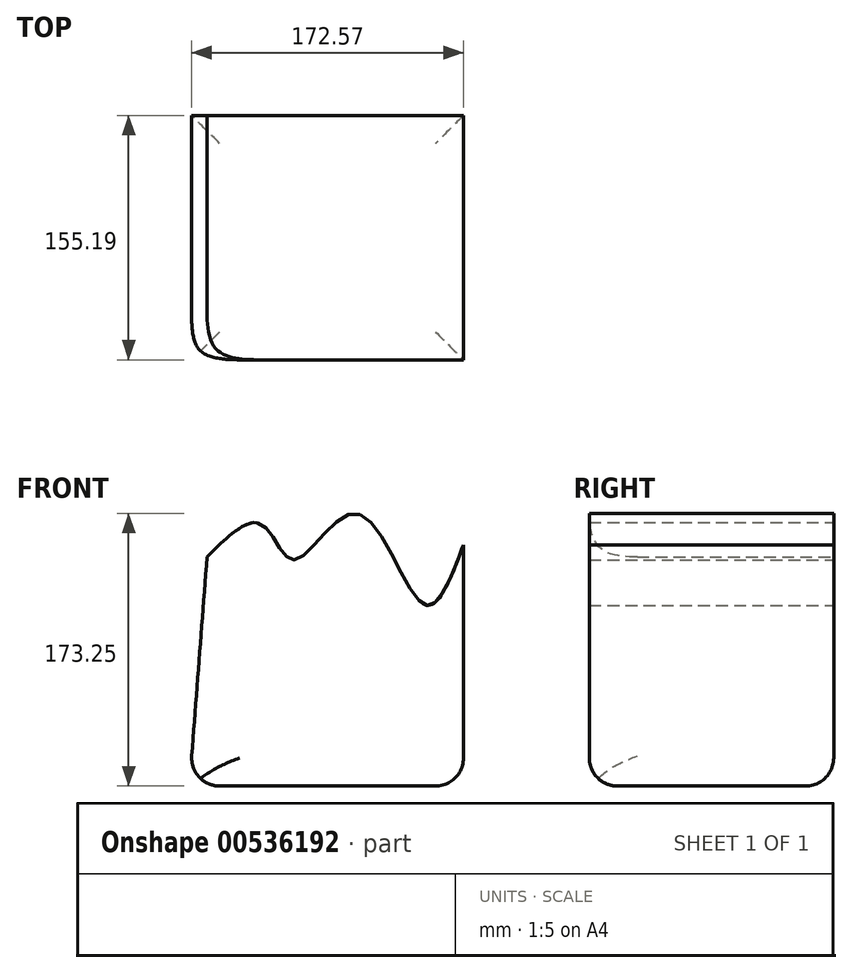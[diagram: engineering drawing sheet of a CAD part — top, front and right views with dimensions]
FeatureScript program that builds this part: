
annotation { "Feature Type Name" : "Feature", "Feature Type Description" : "" }
export const myFeature = defineFeature(function(context is Context, id is Id, definition is map)
    precondition{}
    {
        {
            var Q0;
            Q0=qCreatedBy(makeId("Front.planeOp"),FACE);
            var sketch = newSketch(context, id + "F0", { "sketchPlane" : qUnion([Q0])});
            skFitSpline(sketch, "E0", {"points": [v(-120.22, 34.32) * mm, v(-85.27, 54.9) * mm, v(-65, 32.43) * mm, v(-25.51, 62) * mm, v(17.12, 4.42) * mm, v(42.64, 41.84) * mm], "startDerivative": vector(209.05, 207.88) * mm, "endDerivative": vector(122.06, 324.77) * mm});
            skLineSegment(sketch, "E1", {"start": v(42.64, 41.84) * mm, "end": v(42.64, -111.18) * mm});
            skLineSegment(sketch, "E2", {"start": v(42.64, -111.18) * mm, "end": v(-131.34, -111.18) * mm});
            skLineSegment(sketch, "E3", {"start": v(-131.34, -111.18) * mm, "end": v(-120.22, 34.32) * mm});
            skSolve(sketch);
        }
        {
            var Q0;
            Q0=makeQuery(id+"F0.imprint","IMPRINT",FACE,{"disambiguationData":[TD([[makeQuery(id+"F0.imprint","IMPRINT",EDGE,{"derivedFrom":sQuery(id+"F0.wireOp",EDGE,"E0")}),-1.0]])]});
            extrude(context, id + "F1", {"entities" : qUnion([Q0]), "depth" : 155.2 * mm, "offsetDistance" : 25.4 * mm});
        }
        {
            var Q0;
            Q0=makeQuery(id+"F1.opExtrude","CAP_EDGE",EDGE,{"disambiguationData":[OSD([sQuery(id+"F0.wireOp",EDGE,"E2")])],"isStart":false});
            var Q1;
            Q1=makeQuery(id+"F1.opExtrude","SWEPT_EDGE",EDGE,{"disambiguationData":[OSD([sQuery(id+"F0.wireOp",EDGE,"E1"),sQuery(id+"F0.wireOp",EDGE,"E2")])]});
            var Q2;
            Q2=makeQuery(id+"F1.opExtrude","CAP_EDGE",EDGE,{"disambiguationData":[OSD([sQuery(id+"F0.wireOp",EDGE,"E2")])],"isStart":true});
            var Q3;
            Q3=makeQuery(id+"F1.opExtrude","SWEPT_EDGE",EDGE,{"disambiguationData":[OSD([sQuery(id+"F0.wireOp",EDGE,"E2"),sQuery(id+"F0.wireOp",EDGE,"E3")])]});
            fillet(context, id + "F2", {"entities" : qUnion([Q0, Q1, Q2, Q3]), "radius" : 17.78 * mm, "tangentPropagation" : true, "allowEdgeOverflow" : false});
        }
        {
            var Q0;
            Q0=makeQuery(id+"F1.opExtrude","CAP_EDGE",EDGE,{"disambiguationData":[OSD([sQuery(id+"F0.wireOp",EDGE,"E3")])],"isStart":false});
            fillet(context, id + "F3", {"entities" : qUnion([Q0]), "radius" : 30.48 * mm, "rho" : 0.6, "crossSection" : FilletCrossSection.CONIC, "allowEdgeOverflow" : false});
        }
    });
